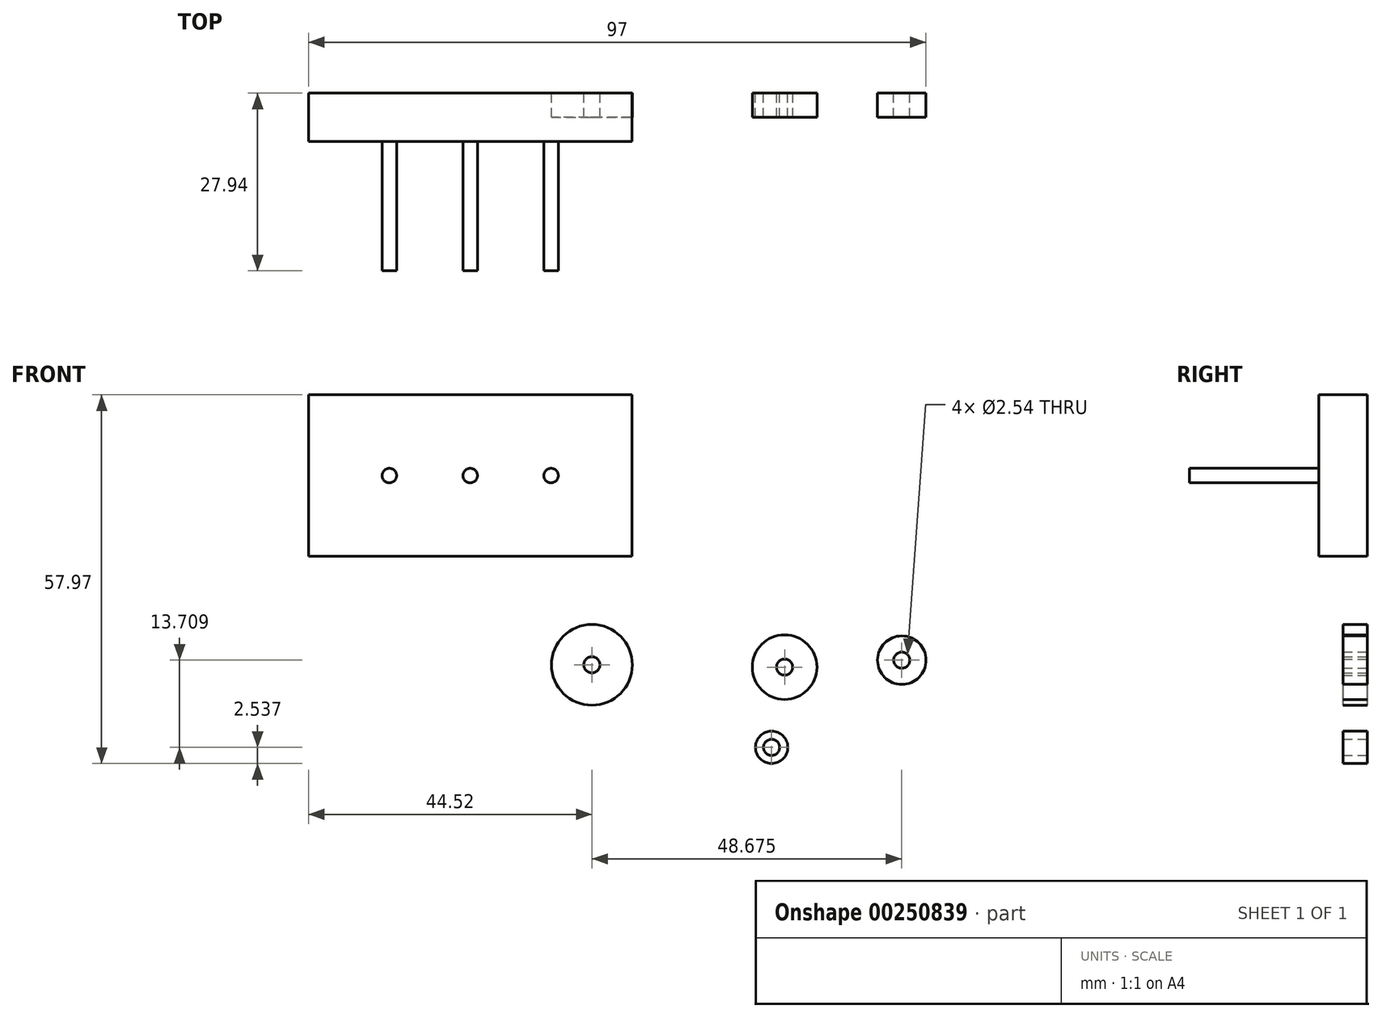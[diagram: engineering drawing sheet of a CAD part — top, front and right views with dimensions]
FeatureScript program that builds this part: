
annotation { "Feature Type Name" : "Feature", "Feature Type Description" : "" }
export const myFeature = defineFeature(function(context is Context, id is Id, definition is map)
    precondition{}
    {
        {
            var Q0;
            Q0=qCreatedBy(makeId("Front.planeOp"),FACE);
            var sketch = newSketch(context, id + "F0", { "sketchPlane" : qUnion([Q0])});
            skCircle(sketch, "E0", {"center": v(0, 0) * mm, "radius": 6.35 * mm});
            skCircle(sketch, "E1", {"center": v(0, 0) * mm, "radius": 1.27 * mm});
            skCircle(sketch, "E2", {"center": v(30.27, -0.36) * mm, "radius": 5.08 * mm});
            skCircle(sketch, "E3", {"center": v(30.27, -0.36) * mm, "radius": 1.27 * mm});
            skCircle(sketch, "E4", {"center": v(48.67, 0.74) * mm, "radius": 3.81 * mm});
            skCircle(sketch, "E5", {"center": v(48.67, 0.74) * mm, "radius": 1.27 * mm});
            skCircle(sketch, "E6", {"center": v(28.23, -12.97) * mm, "radius": 2.54 * mm});
            skCircle(sketch, "E7", {"center": v(28.23, -12.97) * mm, "radius": 1.27 * mm});
            skLineSegment(sketch, "E8.bottom", {"start": v(-44.52, 17.06) * mm, "end": v(6.28, 17.06) * mm});
            skLineSegment(sketch, "E8.top", {"start": v(-44.52, 42.46) * mm, "end": v(6.28, 42.46) * mm});
            skLineSegment(sketch, "E8.left", {"start": v(-44.52, 17.06) * mm, "end": v(-44.52, 42.46) * mm});
            skLineSegment(sketch, "E8.right", {"start": v(6.28, 17.06) * mm, "end": v(6.28, 42.46) * mm});
            skCircle(sketch, "E9", {"center": v(-19.12, 29.76) * mm, "radius": 1.14 * mm});
            skPoint(sketch, "E9.centerSnap0", {"position": v(6.28, 29.76) * mm});
            skPoint(sketch, "E9.centerSnap1", {"position": v(-19.12, 17.06) * mm});
            skLineSegment(sketch, "E10", {"start": v(-44.52, 17.06) * mm, "end": v(-31.82, 17.06) * mm});
            skCircle(sketch, "E11", {"center": v(-31.82, 29.76) * mm, "radius": 1.14 * mm});
            skLineSegment(sketch, "E12", {"start": v(6.28, 17.06) * mm, "end": v(-6.42, 17.06) * mm});
            skCircle(sketch, "E13", {"center": v(-6.42, 29.76) * mm, "radius": 1.14 * mm});
            skSolve(sketch);
        }
        {
            var Q0;
            Q0=makeQuery(id+"F0.imprint","IMPRINT",FACE,{"disambiguationData":[TD([[makeQuery(id+"F0.imprint","IMPRINT",EDGE,{"derivedFrom":sQuery(id+"F0.wireOp",EDGE,"E8.bottom")}),1.0]])]});
            var Q1;
            Q1=makeQuery(id+"F0.imprint","IMPRINT",FACE,{"disambiguationData":[TD([[makeQuery(id+"F0.imprint","IMPRINT",EDGE,{"derivedFrom":sQuery(id+"F0.wireOp",EDGE,"E13")}),1.0]])]});
            var Q2;
            Q2=makeQuery(id+"F0.imprint","IMPRINT",FACE,{"disambiguationData":[TD([[makeQuery(id+"F0.imprint","IMPRINT",EDGE,{"derivedFrom":sQuery(id+"F0.wireOp",EDGE,"E9")}),1.0]])]});
            var Q3;
            Q3=makeQuery(id+"F0.imprint","IMPRINT",FACE,{"disambiguationData":[TD([[makeQuery(id+"F0.imprint","IMPRINT",EDGE,{"derivedFrom":sQuery(id+"F0.wireOp",EDGE,"E11")}),1.0]])]});
            extrude(context, id + "F1", {"entities" : qUnion([Q0, Q1, Q2, Q3]), "depth" : 7.62 * mm});
        }
        {
            var Q0;
            Q0=makeQuery(id+"F0.imprint","IMPRINT",FACE,{"disambiguationData":[TD([[makeQuery(id+"F0.imprint","IMPRINT",EDGE,{"derivedFrom":sQuery(id+"F0.wireOp",EDGE,"E4")}),1.0]])]});
            var Q1;
            Q1=makeQuery(id+"F0.imprint","IMPRINT",FACE,{"disambiguationData":[TD([[makeQuery(id+"F0.imprint","IMPRINT",EDGE,{"derivedFrom":sQuery(id+"F0.wireOp",EDGE,"E2")}),1.0]])]});
            var Q2;
            Q2=makeQuery(id+"F0.imprint","IMPRINT",FACE,{"disambiguationData":[TD([[makeQuery(id+"F0.imprint","IMPRINT",EDGE,{"derivedFrom":sQuery(id+"F0.wireOp",EDGE,"E0")}),1.0]])]});
            var Q3;
            Q3=makeQuery(id+"F0.imprint","IMPRINT",FACE,{"disambiguationData":[TD([[makeQuery(id+"F0.imprint","IMPRINT",EDGE,{"derivedFrom":sQuery(id+"F0.wireOp",EDGE,"E6")}),1.0]])]});
            extrude(context, id + "F2", {"entities" : qUnion([Q0, Q1, Q2, Q3]), "depth" : 3.8 * mm});
        }
        {
            var Q0;
            Q0=makeQuery(id+"F0.imprint","IMPRINT",FACE,{"disambiguationData":[TD([[makeQuery(id+"F0.imprint","IMPRINT",EDGE,{"derivedFrom":sQuery(id+"F0.wireOp",EDGE,"E13")}),1.0]])]});
            var Q1;
            Q1=makeQuery(id+"F0.imprint","IMPRINT",FACE,{"disambiguationData":[TD([[makeQuery(id+"F0.imprint","IMPRINT",EDGE,{"derivedFrom":sQuery(id+"F0.wireOp",EDGE,"E9")}),1.0]])]});
            var Q2;
            Q2=makeQuery(id+"F0.imprint","IMPRINT",FACE,{"disambiguationData":[TD([[makeQuery(id+"F0.imprint","IMPRINT",EDGE,{"derivedFrom":sQuery(id+"F0.wireOp",EDGE,"E11")}),1.0]])]});
            extrude(context, id + "F3", {"entities" : qUnion([Q0, Q1, Q2]), "operationType" : NewBodyOperationType.ADD, "depth" : 27.94 * mm});
        }
    });
